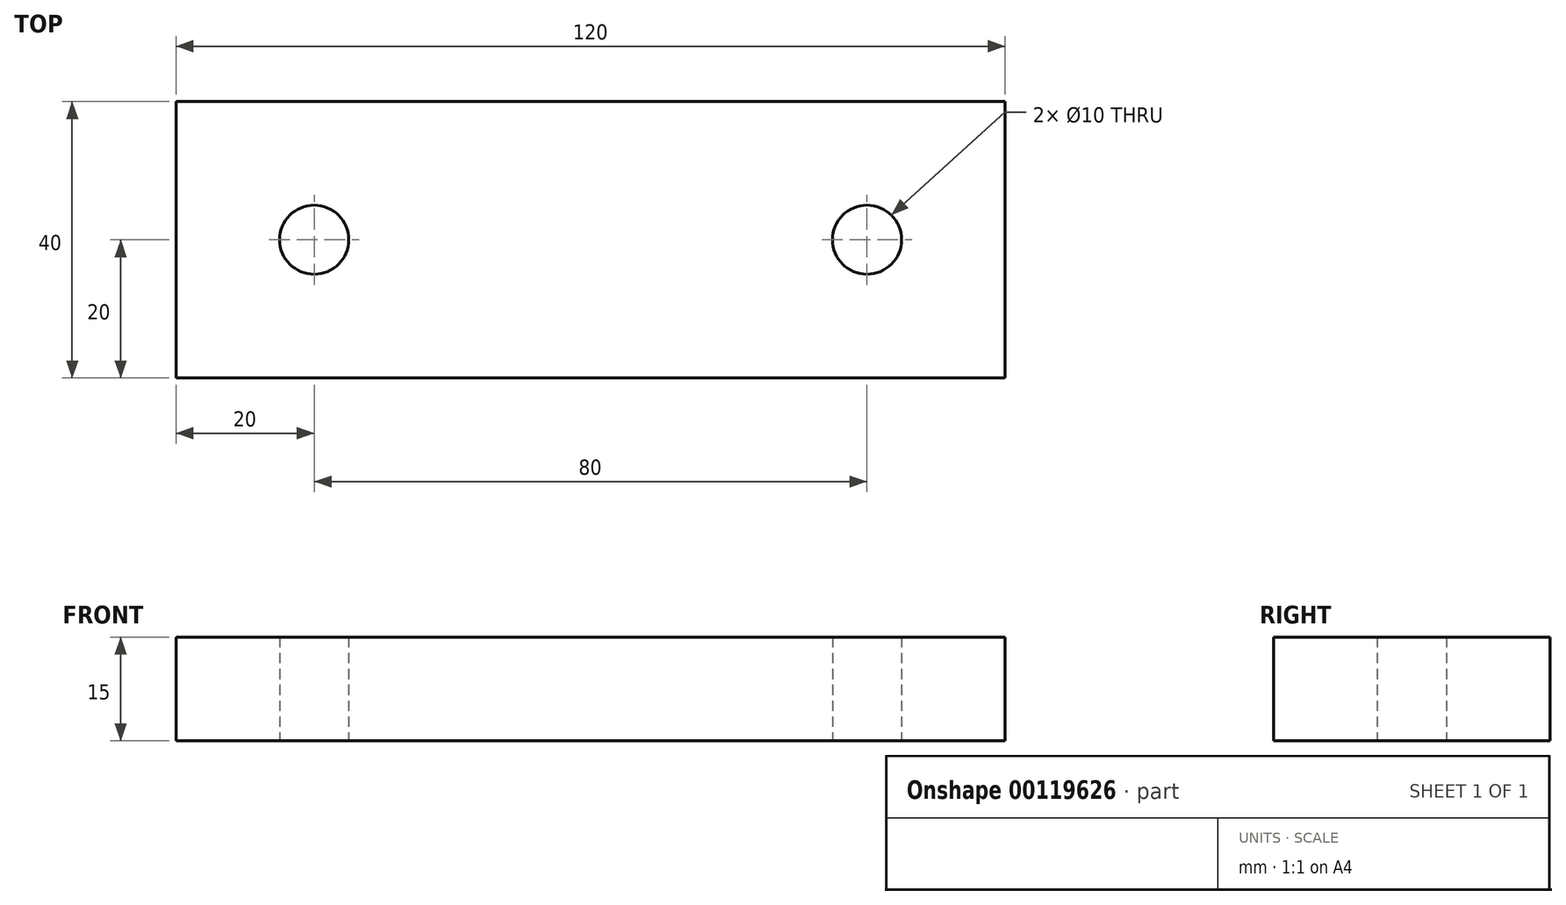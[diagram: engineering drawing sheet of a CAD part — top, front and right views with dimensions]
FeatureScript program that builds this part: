
annotation { "Feature Type Name" : "Feature", "Feature Type Description" : "" }
export const myFeature = defineFeature(function(context is Context, id is Id, definition is map)
    precondition{}
    {
        {
            var Q0;
            Q0=qCreatedBy(makeId("Front.planeOp"),FACE);
            var sketch = newSketch(context, id + "F0", { "sketchPlane" : qUnion([Q0])});
            skLineSegment(sketch, "E0.bottom", {"start": v(0, 0) * mm, "end": v(120, 0) * mm});
            skLineSegment(sketch, "E0.top", {"start": v(0, 15) * mm, "end": v(120, 15) * mm});
            skLineSegment(sketch, "E0.left", {"start": v(0, 0) * mm, "end": v(0, 15) * mm});
            skLineSegment(sketch, "E0.right", {"start": v(120, 0) * mm, "end": v(120, 15) * mm});
            skSolve(sketch);
        }
        {
            var Q0;
            Q0=makeQuery(id+"F0.imprint","IMPRINT",FACE,{"disambiguationData":[TD([[makeQuery(id+"F0.imprint","IMPRINT",EDGE,{"derivedFrom":sQuery(id+"F0.wireOp",EDGE,"E0.bottom")}),1.0]])]});
            extrude(context, id + "F1", {"entities" : qUnion([Q0]), "oppositeDirection" : true, "depth" : 40 * mm});
        }
        {
            var Q0;
            Q0=qCreatedBy(makeId("Top.planeOp"),FACE);
            var sketch = newSketch(context, id + "F2", { "sketchPlane" : qUnion([Q0])});
            skCircle(sketch, "E1", {"center": v(20, 20) * mm, "radius": 5 * mm});
            skCircle(sketch, "E2", {"center": v(100, 20) * mm, "radius": 5 * mm});
            skSolve(sketch);
        }
        {
            var Q0;
            Q0=makeQuery(id+"F2.imprint","IMPRINT",FACE,{"disambiguationData":[TD([[makeQuery(id+"F2.imprint","IMPRINT",EDGE,{"derivedFrom":sQuery(id+"F2.wireOp",EDGE,"E1")}),1.0]])]});
            var Q1;
            Q1=makeQuery(id+"F2.imprint","IMPRINT",FACE,{"disambiguationData":[TD([[makeQuery(id+"F2.imprint","IMPRINT",EDGE,{"derivedFrom":sQuery(id+"F2.wireOp",EDGE,"E2")}),1.0]])]});
            extrude(context, id + "F3", {"entities" : qUnion([Q0, Q1]), "operationType" : NewBodyOperationType.REMOVE, "endBound" : BoundingType.THROUGH_ALL, "depth" : 25 * mm});
        }
    });
